# Revit family: VIESSMANN - Vitocell 100-B (CVB.CVBB)
name_source: partatom
category: Wyposażenie mechaniczne
revit_build: Autodesk Revit 2017 (Build: 20160720_1515(x64)
units: mm (PartAtom-declared; Revit-internal decimal feet)

## family parameters
Numer OmniClass = 23.65.35.11.11
Oparty na płaszczyźnie roboczej = Nie
Punkt obliczania pomieszczeń = Nie
Tnij formami wycięć po wczytaniu = Tak
Typ części = Normalny
Tytuł OmniClass = Storage Water Heaters
Współdzielony = Nie
Wymiar okrągłego złącza = Użyj średnicy
Zawsze pionowo = Tak

## types (5) — shared parameters
Autor = https://www.archispace.pl
Klasa efektywności energetycznej = B
Numer identyfikacyjny produktu = 9W241/11-13MC/E
Opis = Podgrzewacz pojemnościowy
Opis indeksowy = 9W241/11-13MC/E
Producent = Viessmann Sp.z.o.o.
Przepływ objętościowy wody grzewczej (dla podanych wydajności stałych) = 3.00 m³/h
Przepływ po stronie wody grzewczej - dolna wężownica = 3.00 m³/h
Przepływ po stronie wody grzewczej - górna wężownica = 3.00 m³/h
Przyłącza - górna wężownica grzewcza = 1"
URL = https://www.viessmann-projektant.pl
Viessmann Kolor 1 = Viessmann Kolor 1
Viessmann Kolor 2 = Viessmann Kolor 2
Viessmann Kolor 3 = Viessmann Kolor 3

## per-type parameters (varying)
- Zbiornik CVBB 950L: Całkowita masa eksploatacyjna z grzałką elektryczną=1342.00 kg; Ciepła woda użytkowa=1 1/4"; Cyrkulacja=1 1/4"; Czas podgrzewu cwu przy tempraturze zasilania wodą grzewczą 70℃=28 min; Czas podgrzewu cwu przy tempraturze zasilania wodą grzewczą 80℃=22 min; Czas podgrzewu cwu przy tempraturze zasilania wodą grzewczą 90℃=18 min; Ilość ciepła dyżurnego=2.48 kWh/24h; Maks. ilość pobierana przy temperaturze na zasilaniu wodą grzewczą 70℃=55; Maks. ilość pobierana przy temperaturze na zasilaniu wodą grzewczą 80℃=60; Maks. ilość pobierana przy temperaturze na zasilaniu wodą grzewczą 90℃=60; Masa całkowita z izolacją cieplną=390.00 kg; Model=Podgrzewacz pojemnościowy Viessmann Vitocell 100-B CVBB 950L / Hot water storage tank Viessmann Vitocell 100-B CVBB 950L; Objętość wody grzewczej - wężownica dolna=33.1 L; Objętość wody grzewczej - wężownica górna=18.6 L; Opory przepływu po stronie wody grzewczej - dolna wężownica=7600.0 Pa; Opory przepływu po stronie wody grzewczej - górna wężownica=19000.0 Pa; Opory przepływu po stronie wody użytkowej=16000.0 Pa; Podział=1062 mm  [stored 3.48425 ft]; Pojemność czesci solarnej Vsol=450 m³; Pojemność części dyżurnej Vaux=500 m³; Pojemność podgrzewacza=950.0 L; Powierzchnia grzewcza - wężownica dolna=3.9 m²; Powierzchnia grzewcza - wężownica górna=2.2 m²; Przepływ objętościowy wody grzewczej (przy podgrzewie cwu z 10 na 45℃) przy temperaturze na zasilaniu wodą grzewczą 50℃ - wężownica dolna=1.03; Przepływ objętościowy wody grzewczej (przy podgrzewie cwu z 10 na 45℃) przy temperaturze na zasilaniu wodą grzewczą 50℃ - wężownica górna=0.76; Przepływ objętościowy wody grzewczej (przy podgrzewie cwu z 10 na 45℃) przy temperaturze na zasilaniu wodą grzewczą 60℃ - wężownica dolna=1.37; Przepływ objętościowy wody grzewczej (przy podgrzewie cwu z 10 na 45℃) przy temperaturze na zasilaniu wodą grzewczą 60℃ - wężownica górna=1.02; Przepływ objętościowy wody grzewczej (przy podgrzewie cwu z 10 na 45℃) przy temperaturze na zasilaniu wodą grzewczą 70℃ - wężownica dolna=1.93; Przepływ objętościowy wody grzewczej (przy podgrzewie cwu z 10 na 45℃) przy temperaturze na zasilaniu wodą grzewczą 70℃ - wężownica górna=1.43; Przepływ objętościowy wody grzewczej (przy podgrzewie cwu z 10 na 45℃) przy temperaturze na zasilaniu wodą grzewczą 80℃ - wężownica dolna=2.48; Przepływ objętościowy wody grzewczej (przy podgrzewie cwu z 10 na 45℃) przy temperaturze na zasilaniu wodą grzewczą 80℃ - wężownica górna=1.84; Przepływ objętościowy wody grzewczej (przy podgrzewie cwu z 10 na 45℃) przy temperaturze na zasilaniu wodą grzewczą 90℃ - wężownica dolna=3.00; Przepływ objętościowy wody grzewczej (przy podgrzewie cwu z 10 na 45℃) przy temperaturze na zasilaniu wodą grzewczą 90℃ - wężownica górna=2.22; Przepływ objętościowy wody grzewczej (przy podgrzewie cwu z 10 na 60℃) przy temperaturze na zasilaniu wodą grzewczą 70℃ - wężownica dolna=0.91; Przepływ objętościowy wody grzewczej (przy podgrzewie cwu z 10 na 60℃) przy temperaturze na zasilaniu wodą grzewczą 70℃ - wężownica górna=0.72; Przepływ objętościowy wody grzewczej (przy podgrzewie cwu z 10 na 60℃) przy temperaturze na zasilaniu wodą grzewczą 80℃ - wężownica dolna=1.22; Przepływ objętościowy wody grzewczej (przy podgrzewie cwu z 10 na 60℃) przy temperaturze na zasilaniu wodą grzewczą 80℃ - wężownica górna=0.96; Przepływ objętościowy wody grzewczej (przy podgrzewie cwu z 10 na 60℃) przy temperaturze na zasilaniu wodą grzewczą 90℃ - wężownica dolna=1.47; Przepływ objętościowy wody grzewczej (przy podgrzewie cwu z 10 na 60℃) przy temperaturze na zasilaniu wodą grzewczą 90℃ - wężownica górna=1.16; Przepływ po stronie wody użytkowej=2.22 m³/h; Przyłącza - dolna wężownica grzewcza=1 1/4"; Przyłącza - grzałka elektryczna=0"; Szerokość - bez izolacji cieplnej=1005 mm  [stored 3.29724 ft]; Szerokość - z izolacją cieplną=1110 mm  [stored 3.64173 ft]; Szerokość z izolacją=1110 mm  [stored 3.64173 ft]; Współczynnik mocy NL przy temperaturze na zasilaniu wodą grzewczą 70℃=10; Współczynnik mocy NL przy temperaturze na zasilaniu wodą grzewczą 80℃=11; Współczynnik mocy NL przy temperaturze na zasilaniu wodą grzewczą 90℃=11; Wydajność krótkotrwała przy temperaturze na zasilaniu wodą grzewczą 70℃=550 L/10min; Wydajność krótkotrwała przy temperaturze na zasilaniu wodą grzewczą 80℃=600 L/10min; Wydajność krótkotrwała przy temperaturze na zasilaniu wodą grzewczą 90℃=600 L/10min; Wydajność stała (przy podgrzewie cwu z 10 na 45℃) i temperaturze na zasilaniu wodą grzewczą 50℃ - wężownica dolna=42000; Wydajność stała (przy podgrzewie cwu z 10 na 45℃) i temperaturze na zasilaniu wodą grzewczą 50℃ - wężownica górna=31000; Wydajność stała (przy podgrzewie cwu z 10 na 45℃) i temperaturze na zasilaniu wodą grzewczą 60℃ - wężownica dolna=56000; Wydajność stała (przy podgrzewie cwu z 10 na 45℃) i temperaturze na zasilaniu wodą grzewczą 60℃ - wężownica górna=41000; Wydajność stała (przy podgrzewie cwu z 10 na 45℃) i temperaturze na zasilaniu wodą grzewczą 70℃ - wężownica dolna=78000; Wydajność stała (przy podgrzewie cwu z 10 na 45℃) i temperaturze na zasilaniu wodą grzewczą 70℃ - wężownica górna=58000; Wydajność stała (przy podgrzewie cwu z 10 na 45℃) i temperaturze na zasilaniu wodą grzewczą 80℃ - wężownica dolna=101000; Wydajność stała (przy podgrzewie cwu z 10 na 45℃) i temperaturze na zasilaniu wodą grzewczą 80℃ - wężownica górna=75000; Wydajność stała (przy podgrzewie cwu z 10 na 45℃) i temperaturze na zasilaniu wodą grzewczą 90℃ - wężownica dolna=122000; Wydajność stała (przy podgrzewie cwu z 10 na 45℃) i temperaturze na zasilaniu wodą grzewczą 90℃ - wężownica górna=90000; Wydajność stała (przy podgrzewie cwu z 10 na 60℃) i temperaturze na zasilaniu wodą grzewczą 70℃ - wężownica dolna=53000; Wydajność stała (przy podgrzewie cwu z 10 na 60℃) i temperaturze na zasilaniu wodą grzewczą 70℃ - wężownica górna=42000; Wydajność stała (przy podgrzewie cwu z 10 na 60℃) i temperaturze na zasilaniu wodą grzewczą 80℃ - wężownica dolna=71000; Wydajność stała (przy podgrzewie cwu z 10 na 60℃) i temperaturze na zasilaniu wodą grzewczą 80℃ - wężownica górna=56000; Wydajność stała (przy podgrzewie cwu z 10 na 60℃) i temperaturze na zasilaniu wodą grzewczą 90℃ - wężownica dolna=85000; Wydajność stała (przy podgrzewie cwu z 10 na 60℃) i temperaturze na zasilaniu wodą grzewczą 90℃ - wężownica górna=67000; Wymiar przechylenia - bez izolacji cieplnej=2286 mm; Wymiar przechylenia - z izolacją cieplną=0 mm  [stored 0 ft]; Wysokość - bez izolacji cieplnej=2103 mm; Wysokość - z izolacją cieplną=2197 mm; Wysokość króćca cwu=2054 mm; Wysokość króćca cyrkulacji=1278 mm  [stored 4.19291 ft]; Wysokość króćca powrotu wody grzewczej=1130 mm  [stored 3.70735 ft]; Wysokość króćca powrotu wody grzewczej inst. solarnej=363 mm  [stored 1.19094 ft]; Wysokość króćca zasilania wodą grzewczą=1760 mm; Wysokość króćca zasilania wodą grzewczą inst. solarnej=983 mm  [stored 3.22507 ft]; Wysokość króćca zimnej wody użytkowej=73 mm  [stored 0.239501 ft]; Wysokość przyłącza grzałki=501 mm  [stored 1.6437 ft]; Wysokość z izolacją=2197 mm; Zimna woda użytkowa=1 1/4"; Średnica - bez izolacji cieplnej=790 mm  [stored 2.59186 ft]; Średnica - z izolacją cieplną=1062 mm  [stored 3.48425 ft]; Średnica z izolacją cieplną=1062 mm  [stored 3.48425 ft]
- Zbiornik CVBB 300L: Całkowita masa eksploatacyjna z grzałką elektryczną=468.00 kg; Ciepła woda użytkowa=1"; Cyrkulacja=1"; Czas podgrzewu cwu przy tempraturze zasilania wodą grzewczą 70℃=30 min; Czas podgrzewu cwu przy tempraturze zasilania wodą grzewczą 80℃=22 min; Czas podgrzewu cwu przy tempraturze zasilania wodą grzewczą 90℃=16 min; Ilość ciepła dyżurnego=1.65 kWh/24h; Maks. ilość pobierana przy temperaturze na zasilaniu wodą grzewczą 70℃=16; Maks. ilość pobierana przy temperaturze na zasilaniu wodą grzewczą 80℃=17; Maks. ilość pobierana przy temperaturze na zasilaniu wodą grzewczą 90℃=17; Masa całkowita z izolacją cieplną=160.00 kg; Model=Podgrzewacz pojemnościowy Viessmann Vitocell 100-B CVBB 300L / Hot water storage tank Viessmann Vitocell 100-B CVBB 300L; Objętość wody grzewczej - wężownica dolna=10.0 L; Objętość wody grzewczej - wężownica górna=6.0 L; Opory przepływu po stronie wody grzewczej - dolna wężownica=18000.0 Pa; Opory przepływu po stronie wody grzewczej - górna wężownica=13000.0 Pa; Opory przepływu po stronie wody użytkowej=200.0 Pa; Podział=667 mm  [stored 2.18832 ft]; Pojemność czesci solarnej Vsol=173 m³; Pojemność części dyżurnej Vaux=127 m³; Pojemność podgrzewacza=300.0 L; Powierzchnia grzewcza - wężownica dolna=1.5 m²; Powierzchnia grzewcza - wężownica górna=0.9 m²; Przepływ objętościowy wody grzewczej (przy podgrzewie cwu z 10 na 45℃) przy temperaturze na zasilaniu wodą grzewczą 50℃ - wężownica dolna=0.44; Przepływ objętościowy wody grzewczej (przy podgrzewie cwu z 10 na 45℃) przy temperaturze na zasilaniu wodą grzewczą 50℃ - wężownica górna=0.27; Przepływ objętościowy wody grzewczej (przy podgrzewie cwu z 10 na 45℃) przy temperaturze na zasilaniu wodą grzewczą 60℃ - wężownica dolna=0.57; Przepływ objętościowy wody grzewczej (przy podgrzewie cwu z 10 na 45℃) przy temperaturze na zasilaniu wodą grzewczą 60℃ - wężownica górna=0.37; Przepływ objętościowy wody grzewczej (przy podgrzewie cwu z 10 na 45℃) przy temperaturze na zasilaniu wodą grzewczą 70℃ - wężownica dolna=0.81; Przepływ objętościowy wody grzewczej (przy podgrzewie cwu z 10 na 45℃) przy temperaturze na zasilaniu wodą grzewczą 70℃ - wężownica górna=0.49; Przepływ objętościowy wody grzewczej (przy podgrzewie cwu z 10 na 45℃) przy temperaturze na zasilaniu wodą grzewczą 80℃ - wężownica dolna=1.08; Przepływ objętościowy wody grzewczej (przy podgrzewie cwu z 10 na 45℃) przy temperaturze na zasilaniu wodą grzewczą 80℃ - wężownica górna=0.64; Przepływ objętościowy wody grzewczej (przy podgrzewie cwu z 10 na 45℃) przy temperaturze na zasilaniu wodą grzewczą 90℃ - wężownica dolna=1.30; Przepływ objętościowy wody grzewczej (przy podgrzewie cwu z 10 na 45℃) przy temperaturze na zasilaniu wodą grzewczą 90℃ - wężownica górna=0.76; Przepływ objętościowy wody grzewczej (przy podgrzewie cwu z 10 na 60℃) przy temperaturze na zasilaniu wodą grzewczą 70℃ - wężownica dolna=395.00; Przepływ objętościowy wody grzewczej (przy podgrzewie cwu z 10 na 60℃) przy temperaturze na zasilaniu wodą grzewczą 70℃ - wężownica górna=258.00; Przepływ objętościowy wody grzewczej (przy podgrzewie cwu z 10 na 60℃) przy temperaturze na zasilaniu wodą grzewczą 80℃ - wężownica dolna=0.58; Przepływ objętościowy wody grzewczej (przy podgrzewie cwu z 10 na 60℃) przy temperaturze na zasilaniu wodą grzewczą 80℃ - wężownica górna=0.34; Przepływ objętościowy wody grzewczej (przy podgrzewie cwu z 10 na 60℃) przy temperaturze na zasilaniu wodą grzewczą 90℃ - wężownica dolna=0.77; Przepływ objętościowy wody grzewczej (przy podgrzewie cwu z 10 na 60℃) przy temperaturze na zasilaniu wodą grzewczą 90℃ - wężownica górna=0.40; Przepływ po stronie wody użytkowej=0.76 m³/h; Przyłącza - dolna wężownica grzewcza=1"; Przyłącza - grzałka elektryczna=1 1/2"; Szerokość - bez izolacji cieplnej=0 mm  [stored 0 ft]; Szerokość - z izolacją cieplną=744 mm  [stored 2.44094 ft]; Szerokość z izolacją=744 mm  [stored 2.44094 ft]; Współczynnik mocy NL przy temperaturze na zasilaniu wodą grzewczą 70℃=1.4; Współczynnik mocy NL przy temperaturze na zasilaniu wodą grzewczą 80℃=1.5; Współczynnik mocy NL przy temperaturze na zasilaniu wodą grzewczą 90℃=1.6; Wydajność krótkotrwała przy temperaturze na zasilaniu wodą grzewczą 70℃=164 L/10min; Wydajność krótkotrwała przy temperaturze na zasilaniu wodą grzewczą 80℃=168 L/10min; Wydajność krótkotrwała przy temperaturze na zasilaniu wodą grzewczą 90℃=173 L/10min; Wydajność stała (przy podgrzewie cwu z 10 na 45℃) i temperaturze na zasilaniu wodą grzewczą 50℃ - wężownica dolna=18000; Wydajność stała (przy podgrzewie cwu z 10 na 45℃) i temperaturze na zasilaniu wodą grzewczą 50℃ - wężownica górna=11000; Wydajność stała (przy podgrzewie cwu z 10 na 45℃) i temperaturze na zasilaniu wodą grzewczą 60℃ - wężownica dolna=23000; Wydajność stała (przy podgrzewie cwu z 10 na 45℃) i temperaturze na zasilaniu wodą grzewczą 60℃ - wężownica górna=15000; Wydajność stała (przy podgrzewie cwu z 10 na 45℃) i temperaturze na zasilaniu wodą grzewczą 70℃ - wężownica dolna=33000; Wydajność stała (przy podgrzewie cwu z 10 na 45℃) i temperaturze na zasilaniu wodą grzewczą 70℃ - wężownica górna=20000; Wydajność stała (przy podgrzewie cwu z 10 na 45℃) i temperaturze na zasilaniu wodą grzewczą 80℃ - wężownica dolna=44000; Wydajność stała (przy podgrzewie cwu z 10 na 45℃) i temperaturze na zasilaniu wodą grzewczą 80℃ - wężownica górna=26000; Wydajność stała (przy podgrzewie cwu z 10 na 45℃) i temperaturze na zasilaniu wodą grzewczą 90℃ - wężownica dolna=53000; Wydajność stała (przy podgrzewie cwu z 10 na 45℃) i temperaturze na zasilaniu wodą grzewczą 90℃ - wężownica górna=31000; Wydajność stała (przy podgrzewie cwu z 10 na 60℃) i temperaturze na zasilaniu wodą grzewczą 70℃ - wężownica dolna=23000; Wydajność stała (przy podgrzewie cwu z 10 na 60℃) i temperaturze na zasilaniu wodą grzewczą 70℃ - wężownica górna=15000; Wydajność stała (przy podgrzewie cwu z 10 na 60℃) i temperaturze na zasilaniu wodą grzewczą 80℃ - wężownica dolna=34000; Wydajność stała (przy podgrzewie cwu z 10 na 60℃) i temperaturze na zasilaniu wodą grzewczą 80℃ - wężownica górna=20000; Wydajność stała (przy podgrzewie cwu z 10 na 60℃) i temperaturze na zasilaniu wodą grzewczą 90℃ - wężownica dolna=45000; Wydajność stała (przy podgrzewie cwu z 10 na 60℃) i temperaturze na zasilaniu wodą grzewczą 90℃ - wężownica górna=23000; Wymiar przechylenia - bez izolacji cieplnej=0 mm  [stored 0 ft]; Wymiar przechylenia - z izolacją cieplną=1825 mm; Wysokość - bez izolacji cieplnej=0 mm  [stored 0 ft]; Wysokość - z izolacją cieplną=1734 mm; Wysokość króćca cwu=1600 mm; Wysokość króćca cyrkulacji=1115 mm  [stored 3.65814 ft]; Wysokość króćca powrotu wody grzewczej=995 mm  [stored 3.26444 ft]; Wysokość króćca powrotu wody grzewczej inst. solarnej=260 mm  [stored 0.853018 ft]; Wysokość króćca zasilania wodą grzewczą=1355 mm  [stored 4.44554 ft]; Wysokość króćca zasilania wodą grzewczą inst. solarnej=875 mm  [stored 2.87073 ft]; Wysokość króćca zimnej wody użytkowej=76 mm  [stored 0.249344 ft]; Wysokość przyłącza grzałki=333 mm  [stored 1.09252 ft]; Wysokość z izolacją=1734 mm; Zimna woda użytkowa=1"; Średnica - bez izolacji cieplnej=0 mm  [stored 0 ft]; Średnica - z izolacją cieplną=667 mm  [stored 2.18832 ft]; Średnica z izolacją cieplną=667 mm  [stored 2.18832 ft]
- Zbiornik CVB 500L: Całkowita masa eksploatacyjna z grzałką elektryczną=707.00 kg; Ciepła woda użytkowa=1 1/4"; Cyrkulacja=1"; Czas podgrzewu cwu przy tempraturze zasilania wodą grzewczą 70℃=37 min; Czas podgrzewu cwu przy tempraturze zasilania wodą grzewczą 80℃=24 min; Czas podgrzewu cwu przy tempraturze zasilania wodą grzewczą 90℃=19 min; Ilość ciepła dyżurnego=1.95 kWh/24h; Maks. ilość pobierana przy temperaturze na zasilaniu wodą grzewczą 70℃=30; Maks. ilość pobierana przy temperaturze na zasilaniu wodą grzewczą 80℃=32; Maks. ilość pobierana przy temperaturze na zasilaniu wodą grzewczą 90℃=32; Masa całkowita z izolacją cieplną=205.00 kg; Model=Podgrzewacz pojemnościowy Viessmann Vitocell 100-B CVB 500L / Hot water storage tank Viessmann Vitocell 100-B CVB 500L; Objętość wody grzewczej - wężownica dolna=12.5 L; Objętość wody grzewczej - wężownica górna=9.0 L; Opory przepływu po stronie wody grzewczej - dolna wężownica=20000.0 Pa; Opory przepływu po stronie wody grzewczej - górna wężownica=18000.0 Pa; Opory przepływu po stronie wody użytkowej=250.0 Pa; Podział=859 mm  [stored 2.81824 ft]; Pojemność czesci solarnej Vsol=269 m³; Pojemność części dyżurnej Vaux=231 m³; Pojemność podgrzewacza=500.0 L; Powierzchnia grzewcza - wężownica dolna=1.9 m²; Powierzchnia grzewcza - wężownica górna=1.4 m²; Przepływ objętościowy wody grzewczej (przy podgrzewie cwu z 10 na 45℃) przy temperaturze na zasilaniu wodą grzewczą 50℃ - wężownica dolna=0.59; Przepływ objętościowy wody grzewczej (przy podgrzewie cwu z 10 na 45℃) przy temperaturze na zasilaniu wodą grzewczą 50℃ - wężownica górna=0.39; Przepływ objętościowy wody grzewczej (przy podgrzewie cwu z 10 na 45℃) przy temperaturze na zasilaniu wodą grzewczą 60℃ - wężownica dolna=0.79; Przepływ objętościowy wody grzewczej (przy podgrzewie cwu z 10 na 45℃) przy temperaturze na zasilaniu wodą grzewczą 60℃ - wężownica górna=0.54; Przepływ objętościowy wody grzewczej (przy podgrzewie cwu z 10 na 45℃) przy temperaturze na zasilaniu wodą grzewczą 70℃ - wężownica dolna=1.11; Przepływ objętościowy wody grzewczej (przy podgrzewie cwu z 10 na 45℃) przy temperaturze na zasilaniu wodą grzewczą 70℃ - wężownica górna=0.74; Przepływ objętościowy wody grzewczej (przy podgrzewie cwu z 10 na 45℃) przy temperaturze na zasilaniu wodą grzewczą 80℃ - wężownica dolna=1.43; Przepływ objętościowy wody grzewczej (przy podgrzewie cwu z 10 na 45℃) przy temperaturze na zasilaniu wodą grzewczą 80℃ - wężownica górna=0.98; Przepływ objętościowy wody grzewczej (przy podgrzewie cwu z 10 na 45℃) przy temperaturze na zasilaniu wodą grzewczą 90℃ - wężownica dolna=1.72; Przepływ objętościowy wody grzewczej (przy podgrzewie cwu z 10 na 45℃) przy temperaturze na zasilaniu wodą grzewczą 90℃ - wężownica górna=1.15; Przepływ objętościowy wody grzewczej (przy podgrzewie cwu z 10 na 60℃) przy temperaturze na zasilaniu wodą grzewczą 70℃ - wężownica dolna=0.57; Przepływ objętościowy wody grzewczej (przy podgrzewie cwu z 10 na 60℃) przy temperaturze na zasilaniu wodą grzewczą 70℃ - wężownica górna=0.38; Przepływ objętościowy wody grzewczej (przy podgrzewie cwu z 10 na 60℃) przy temperaturze na zasilaniu wodą grzewczą 80℃ - wężownica dolna=0.76; Przepływ objętościowy wody grzewczej (przy podgrzewie cwu z 10 na 60℃) przy temperaturze na zasilaniu wodą grzewczą 80℃ - wężownica górna=0.52; Przepływ objętościowy wody grzewczej (przy podgrzewie cwu z 10 na 60℃) przy temperaturze na zasilaniu wodą grzewczą 90℃ - wężownica dolna=0.91; Przepływ objętościowy wody grzewczej (przy podgrzewie cwu z 10 na 60℃) przy temperaturze na zasilaniu wodą grzewczą 90℃ - wężownica górna=0.62; Przepływ po stronie wody użytkowej=1.15 m³/h; Przyłącza - dolna wężownica grzewcza=1"; Przyłącza - grzałka elektryczna=1 1/2"; Szerokość - bez izolacji cieplnej=881 mm  [stored 2.89042 ft]; Szerokość - z izolacją cieplną=923 mm  [stored 3.02822 ft]; Szerokość z izolacją=923 mm  [stored 3.02822 ft]; Współczynnik mocy NL przy temperaturze na zasilaniu wodą grzewczą 70℃=5; Współczynnik mocy NL przy temperaturze na zasilaniu wodą grzewczą 80℃=6; Współczynnik mocy NL przy temperaturze na zasilaniu wodą grzewczą 90℃=6; Wydajność krótkotrwała przy temperaturze na zasilaniu wodą grzewczą 70℃=299 L/10min; Wydajność krótkotrwała przy temperaturze na zasilaniu wodą grzewczą 80℃=319 L/10min; Wydajność krótkotrwała przy temperaturze na zasilaniu wodą grzewczą 90℃=319 L/10min; Wydajność stała (przy podgrzewie cwu z 10 na 45℃) i temperaturze na zasilaniu wodą grzewczą 50℃ - wężownica dolna=24000; Wydajność stała (przy podgrzewie cwu z 10 na 45℃) i temperaturze na zasilaniu wodą grzewczą 50℃ - wężownica górna=16000; Wydajność stała (przy podgrzewie cwu z 10 na 45℃) i temperaturze na zasilaniu wodą grzewczą 60℃ - wężownica dolna=32000; Wydajność stała (przy podgrzewie cwu z 10 na 45℃) i temperaturze na zasilaniu wodą grzewczą 60℃ - wężownica górna=22000; Wydajność stała (przy podgrzewie cwu z 10 na 45℃) i temperaturze na zasilaniu wodą grzewczą 70℃ - wężownica dolna=45000; Wydajność stała (przy podgrzewie cwu z 10 na 45℃) i temperaturze na zasilaniu wodą grzewczą 70℃ - wężownica górna=30000; Wydajność stała (przy podgrzewie cwu z 10 na 45℃) i temperaturze na zasilaniu wodą grzewczą 80℃ - wężownica dolna=58000; Wydajność stała (przy podgrzewie cwu z 10 na 45℃) i temperaturze na zasilaniu wodą grzewczą 80℃ - wężownica górna=40000; Wydajność stała (przy podgrzewie cwu z 10 na 45℃) i temperaturze na zasilaniu wodą grzewczą 90℃ - wężownica dolna=70000; Wydajność stała (przy podgrzewie cwu z 10 na 45℃) i temperaturze na zasilaniu wodą grzewczą 90℃ - wężownica górna=47000; Wydajność stała (przy podgrzewie cwu z 10 na 60℃) i temperaturze na zasilaniu wodą grzewczą 70℃ - wężownica dolna=33000; Wydajność stała (przy podgrzewie cwu z 10 na 60℃) i temperaturze na zasilaniu wodą grzewczą 70℃ - wężownica górna=22000; Wydajność stała (przy podgrzewie cwu z 10 na 60℃) i temperaturze na zasilaniu wodą grzewczą 80℃ - wężownica dolna=44000; Wydajność stała (przy podgrzewie cwu z 10 na 60℃) i temperaturze na zasilaniu wodą grzewczą 80℃ - wężownica górna=30000; Wydajność stała (przy podgrzewie cwu z 10 na 60℃) i temperaturze na zasilaniu wodą grzewczą 90℃ - wężownica dolna=53000; Wydajność stała (przy podgrzewie cwu z 10 na 60℃) i temperaturze na zasilaniu wodą grzewczą 90℃ - wężownica górna=36000; Wymiar przechylenia - bez izolacji cieplnej=1860 mm; Wymiar przechylenia - z izolacją cieplną=0 mm  [stored 0 ft]; Wysokość - bez izolacji cieplnej=1844 mm; Wysokość - z izolacją cieplną=1948 mm; Wysokość króćca cwu=1784 mm; Wysokość króćca cyrkulacji=1230 mm  [stored 4.03543 ft]; Wysokość króćca powrotu wody grzewczej=1044 mm; Wysokość króćca powrotu wody grzewczej inst. solarnej=349 mm  [stored 1.14501 ft]; Wysokość króćca zasilania wodą grzewczą=1444 mm  [stored 4.73753 ft]; Wysokość króćca zasilania wodą grzewczą inst. solarnej=924 mm  [stored 3.0315 ft]; Wysokość króćca zimnej wody użytkowej=107 mm  [stored 0.35105 ft]; Wysokość przyłącza grzałki=422 mm  [stored 1.38451 ft]; Wysokość z izolacją=1948 mm; Zimna woda użytkowa=1 1/4"; Średnica - bez izolacji cieplnej=650 mm  [stored 2.13255 ft]; Średnica - z izolacją cieplną=859 mm  [stored 2.81824 ft]; Średnica z izolacją cieplną=859 mm  [stored 2.81824 ft]
- Zbiornik CVB 400L: Całkowita masa eksploatacyjna z grzałką elektryczną=569.00 kg; Ciepła woda użytkowa=1 1/4"; Cyrkulacja=1"; Czas podgrzewu cwu przy tempraturze zasilania wodą grzewczą 70℃=36 min; Czas podgrzewu cwu przy tempraturze zasilania wodą grzewczą 80℃=23 min; Czas podgrzewu cwu przy tempraturze zasilania wodą grzewczą 90℃=17 min; Ilość ciepła dyżurnego=1.80 kWh/24h; Maks. ilość pobierana przy temperaturze na zasilaniu wodą grzewczą 70℃=21; Maks. ilość pobierana przy temperaturze na zasilaniu wodą grzewczą 80℃=23; Maks. ilość pobierana przy temperaturze na zasilaniu wodą grzewczą 90℃=23; Masa całkowita z izolacją cieplną=167.00 kg; Model=Podgrzewacz pojemnościowy Viessmann Vitocell 100-B CVB 400L / Hot water storage tank Viessmann Vitocell 100-B CVB 400L; Objętość wody grzewczej - wężownica dolna=10.5 L; Objętość wody grzewczej - wężownica górna=6.5 L; Opory przepływu po stronie wody grzewczej - dolna wężownica=12000.0 Pa; Opory przepływu po stronie wody grzewczej - górna wężownica=18000.0 Pa; Opory przepływu po stronie wody użytkowej=200.0 Pa; Podział=859 mm  [stored 2.81824 ft]; Pojemność czesci solarnej Vsol=233 m³; Pojemność części dyżurnej Vaux=167 m³; Pojemność podgrzewacza=400.0 L; Powierzchnia grzewcza - wężownica dolna=1.5 m²; Powierzchnia grzewcza - wężownica górna=1.0 m²; Przepływ objętościowy wody grzewczej (przy podgrzewie cwu z 10 na 45℃) przy temperaturze na zasilaniu wodą grzewczą 50℃ - wężownica dolna=0.32; Przepływ objętościowy wody grzewczej (przy podgrzewie cwu z 10 na 45℃) przy temperaturze na zasilaniu wodą grzewczą 50℃ - wężownica górna=0.25; Przepływ objętościowy wody grzewczej (przy podgrzewie cwu z 10 na 45℃) przy temperaturze na zasilaniu wodą grzewczą 60℃ - wężownica dolna=0.66; Przepływ objętościowy wody grzewczej (przy podgrzewie cwu z 10 na 45℃) przy temperaturze na zasilaniu wodą grzewczą 60℃ - wężownica górna=0.42; Przepływ objętościowy wody grzewczej (przy podgrzewie cwu z 10 na 45℃) przy temperaturze na zasilaniu wodą grzewczą 70℃ - wężownica dolna=0.96; Przepływ objętościowy wody grzewczej (przy podgrzewie cwu z 10 na 45℃) przy temperaturze na zasilaniu wodą grzewczą 70℃ - wężownica górna=0.61; Przepływ objętościowy wody grzewczej (przy podgrzewie cwu z 10 na 45℃) przy temperaturze na zasilaniu wodą grzewczą 80℃ - wężownica dolna=1.28; Przepływ objętościowy wody grzewczej (przy podgrzewie cwu z 10 na 45℃) przy temperaturze na zasilaniu wodą grzewczą 80℃ - wężownica górna=0.81; Przepływ objętościowy wody grzewczej (przy podgrzewie cwu z 10 na 45℃) przy temperaturze na zasilaniu wodą grzewczą 90℃ - wężownica dolna=1.55; Przepływ objętościowy wody grzewczej (przy podgrzewie cwu z 10 na 45℃) przy temperaturze na zasilaniu wodą grzewczą 90℃ - wężownica górna=1.03; Przepływ objętościowy wody grzewczej (przy podgrzewie cwu z 10 na 60℃) przy temperaturze na zasilaniu wodą grzewczą 70℃ - wężownica dolna=0.50; Przepływ objętościowy wody grzewczej (przy podgrzewie cwu z 10 na 60℃) przy temperaturze na zasilaniu wodą grzewczą 70℃ - wężownica górna=0.31; Przepływ objętościowy wody grzewczej (przy podgrzewie cwu z 10 na 60℃) przy temperaturze na zasilaniu wodą grzewczą 80℃ - wężownica dolna=0.72; Przepływ objętościowy wody grzewczej (przy podgrzewie cwu z 10 na 60℃) przy temperaturze na zasilaniu wodą grzewczą 80℃ - wężownica górna=0.46; Przepływ objętościowy wody grzewczej (przy podgrzewie cwu z 10 na 60℃) przy temperaturze na zasilaniu wodą grzewczą 90℃ - wężownica dolna=0.96; Przepływ objętościowy wody grzewczej (przy podgrzewie cwu z 10 na 60℃) przy temperaturze na zasilaniu wodą grzewczą 90℃ - wężownica górna=0.62; Przepływ po stronie wody użytkowej=1.03 m³/h; Przyłącza - dolna wężownica grzewcza=1"; Przyłącza - grzałka elektryczna=1 1/2"; Szerokość - bez izolacji cieplnej=881 mm  [stored 2.89042 ft]; Szerokość - z izolacją cieplną=923 mm  [stored 3.02822 ft]; Szerokość z izolacją=923 mm  [stored 3.02822 ft]; Współczynnik mocy NL przy temperaturze na zasilaniu wodą grzewczą 70℃=2.5; Współczynnik mocy NL przy temperaturze na zasilaniu wodą grzewczą 80℃=3; Współczynnik mocy NL przy temperaturze na zasilaniu wodą grzewczą 90℃=3; Wydajność krótkotrwała przy temperaturze na zasilaniu wodą grzewczą 70℃=210 L/10min; Wydajność krótkotrwała przy temperaturze na zasilaniu wodą grzewczą 80℃=230 L/10min; Wydajność krótkotrwała przy temperaturze na zasilaniu wodą grzewczą 90℃=230 L/10min; Wydajność stała (przy podgrzewie cwu z 10 na 45℃) i temperaturze na zasilaniu wodą grzewczą 50℃ - wężownica dolna=13000; Wydajność stała (przy podgrzewie cwu z 10 na 45℃) i temperaturze na zasilaniu wodą grzewczą 50℃ - wężownica górna=10000; Wydajność stała (przy podgrzewie cwu z 10 na 45℃) i temperaturze na zasilaniu wodą grzewczą 60℃ - wężownica dolna=27000; Wydajność stała (przy podgrzewie cwu z 10 na 45℃) i temperaturze na zasilaniu wodą grzewczą 60℃ - wężownica górna=17000; Wydajność stała (przy podgrzewie cwu z 10 na 45℃) i temperaturze na zasilaniu wodą grzewczą 70℃ - wężownica dolna=39000; Wydajność stała (przy podgrzewie cwu z 10 na 45℃) i temperaturze na zasilaniu wodą grzewczą 70℃ - wężownica górna=25000; Wydajność stała (przy podgrzewie cwu z 10 na 45℃) i temperaturze na zasilaniu wodą grzewczą 80℃ - wężownica dolna=52000; Wydajność stała (przy podgrzewie cwu z 10 na 45℃) i temperaturze na zasilaniu wodą grzewczą 80℃ - wężownica górna=33000; Wydajność stała (przy podgrzewie cwu z 10 na 45℃) i temperaturze na zasilaniu wodą grzewczą 90℃ - wężownica dolna=63000; Wydajność stała (przy podgrzewie cwu z 10 na 45℃) i temperaturze na zasilaniu wodą grzewczą 90℃ - wężownica górna=42000; Wydajność stała (przy podgrzewie cwu z 10 na 60℃) i temperaturze na zasilaniu wodą grzewczą 70℃ - wężownica dolna=29000; Wydajność stała (przy podgrzewie cwu z 10 na 60℃) i temperaturze na zasilaniu wodą grzewczą 70℃ - wężownica górna=18000; Wydajność stała (przy podgrzewie cwu z 10 na 60℃) i temperaturze na zasilaniu wodą grzewczą 80℃ - wężownica dolna=42000; Wydajność stała (przy podgrzewie cwu z 10 na 60℃) i temperaturze na zasilaniu wodą grzewczą 80℃ - wężownica górna=27000; Wydajność stała (przy podgrzewie cwu z 10 na 60℃) i temperaturze na zasilaniu wodą grzewczą 90℃ - wężownica dolna=56000; Wydajność stała (przy podgrzewie cwu z 10 na 60℃) i temperaturze na zasilaniu wodą grzewczą 90℃ - wężownica górna=36000; Wymiar przechylenia - bez izolacji cieplnej=1550 mm; Wymiar przechylenia - z izolacją cieplną=0 mm  [stored 0 ft]; Wysokość - bez izolacji cieplnej=1844 mm; Wysokość - z izolacją cieplną=1948 mm; Wysokość króćca cwu=1458 mm  [stored 4.78346 ft]; Wysokość króćca cyrkulacji=1044 mm; Wysokość króćca powrotu wody grzewczej=924 mm  [stored 3.0315 ft]; Wysokość króćca powrotu wody grzewczej inst. solarnej=349 mm  [stored 1.14501 ft]; Wysokość króćca zasilania wodą grzewczą=1204 mm  [stored 3.95013 ft]; Wysokość króćca zasilania wodą grzewczą inst. solarnej=804 mm  [stored 2.6378 ft]; Wysokość króćca zimnej wody użytkowej=107 mm  [stored 0.35105 ft]; Wysokość przyłącza grzałki=422 mm  [stored 1.38451 ft]; Wysokość z izolacją=1624 mm; Zimna woda użytkowa=1 1/4"; Średnica - bez izolacji cieplnej=650 mm  [stored 2.13255 ft]; Średnica - z izolacją cieplną=859 mm  [stored 2.81824 ft]; Średnica z izolacją cieplną=859 mm  [stored 2.81824 ft]
- Zbiornik CVBB 750L: Całkowita masa eksploatacyjna z grzałką elektryczną=1072.00 kg; Ciepła woda użytkowa=1 1/4"; Cyrkulacja=1 1/4"; Czas podgrzewu cwu przy tempraturze zasilania wodą grzewczą 70℃=26 min; Czas podgrzewu cwu przy tempraturze zasilania wodą grzewczą 80℃=21 min; Czas podgrzewu cwu przy tempraturze zasilania wodą grzewczą 90℃=17 min; Ilość ciepła dyżurnego=2.28 kWh/24h; Maks. ilość pobierana przy temperaturze na zasilaniu wodą grzewczą 70℃=40; Maks. ilość pobierana przy temperaturze na zasilaniu wodą grzewczą 80℃=44; Maks. ilość pobierana przy temperaturze na zasilaniu wodą grzewczą 90℃=44; Masa całkowita z izolacją cieplną=320.00 kg; Model=Podgrzewacz pojemnościowy Viessmann Vitocell 100-B CVBB 750L / Hot water storage tank Viessmann Vitocell 100-B CVBB 750L; Objętość wody grzewczej - wężownica dolna=29.7 L; Objętość wody grzewczej - wężownica górna=13.8 L; Opory przepływu po stronie wody grzewczej - dolna wężownica=7600.0 Pa; Opory przepływu po stronie wody grzewczej - górna wężownica=19000.0 Pa; Opory przepływu po stronie wody użytkowej=700.0 Pa; Podział=1062 mm  [stored 3.48425 ft]; Pojemność czesci solarnej Vsol=385 m³; Pojemność części dyżurnej Vaux=365 m³; Pojemność podgrzewacza=750.0 L; Powierzchnia grzewcza - wężownica dolna=3.5 m²; Powierzchnia grzewcza - wężownica górna=1.6 m²; Przepływ objętościowy wody grzewczej (przy podgrzewie cwu z 10 na 45℃) przy temperaturze na zasilaniu wodą grzewczą 50℃ - wężownica dolna=0.96; Przepływ objętościowy wody grzewczej (przy podgrzewie cwu z 10 na 45℃) przy temperaturze na zasilaniu wodą grzewczą 50℃ - wężownica górna=0.64; Przepływ objętościowy wody grzewczej (przy podgrzewie cwu z 10 na 45℃) przy temperaturze na zasilaniu wodą grzewczą 60℃ - wężownica dolna=1.28; Przepływ objętościowy wody grzewczej (przy podgrzewie cwu z 10 na 45℃) przy temperaturze na zasilaniu wodą grzewczą 60℃ - wężownica górna=0.85; Przepływ objętościowy wody grzewczej (przy podgrzewie cwu z 10 na 45℃) przy temperaturze na zasilaniu wodą grzewczą 70℃ - wężownica dolna=1.79; Przepływ objętościowy wody grzewczej (przy podgrzewie cwu z 10 na 45℃) przy temperaturze na zasilaniu wodą grzewczą 70℃ - wężownica górna=1.20; Przepływ objętościowy wody grzewczej (przy podgrzewie cwu z 10 na 45℃) przy temperaturze na zasilaniu wodą grzewczą 80℃ - wężownica dolna=2.31; Przepływ objętościowy wody grzewczej (przy podgrzewie cwu z 10 na 45℃) przy temperaturze na zasilaniu wodą grzewczą 80℃ - wężownica górna=1.55; Przepływ objętościowy wody grzewczej (przy podgrzewie cwu z 10 na 45℃) przy temperaturze na zasilaniu wodą grzewczą 90℃ - wężownica dolna=2.79; Przepływ objętościowy wody grzewczej (przy podgrzewie cwu z 10 na 45℃) przy temperaturze na zasilaniu wodą grzewczą 90℃ - wężownica górna=1.87; Przepływ objętościowy wody grzewczej (przy podgrzewie cwu z 10 na 60℃) przy temperaturze na zasilaniu wodą grzewczą 70℃ - wężownica dolna=0.85; Przepływ objętościowy wody grzewczej (przy podgrzewie cwu z 10 na 60℃) przy temperaturze na zasilaniu wodą grzewczą 70℃ - wężownica górna=0.63; Przepływ objętościowy wody grzewczej (przy podgrzewie cwu z 10 na 60℃) przy temperaturze na zasilaniu wodą grzewczą 80℃ - wężownica dolna=1.13; Przepływ objętościowy wody grzewczej (przy podgrzewie cwu z 10 na 60℃) przy temperaturze na zasilaniu wodą grzewczą 80℃ - wężownica górna=0.84; Przepływ objętościowy wody grzewczej (przy podgrzewie cwu z 10 na 60℃) przy temperaturze na zasilaniu wodą grzewczą 90℃ - wężownica dolna=1.36; Przepływ objętościowy wody grzewczej (przy podgrzewie cwu z 10 na 60℃) przy temperaturze na zasilaniu wodą grzewczą 90℃ - wężownica górna=1.01; Przepływ po stronie wody użytkowej=1.87 m³/h; Przyłącza - dolna wężownica grzewcza=1 1/4"; Przyłącza - grzałka elektryczna=0"; Szerokość - bez izolacji cieplnej=1005 mm  [stored 3.29724 ft]; Szerokość - z izolacją cieplną=1110 mm  [stored 3.64173 ft]; Szerokość z izolacją=1110 mm  [stored 3.64173 ft]; Współczynnik mocy NL przy temperaturze na zasilaniu wodą grzewczą 70℃=7; Współczynnik mocy NL przy temperaturze na zasilaniu wodą grzewczą 80℃=8; Współczynnik mocy NL przy temperaturze na zasilaniu wodą grzewczą 90℃=8; Wydajność krótkotrwała przy temperaturze na zasilaniu wodą grzewczą 70℃=400 L/10min; Wydajność krótkotrwała przy temperaturze na zasilaniu wodą grzewczą 80℃=438 L/10min; Wydajność krótkotrwała przy temperaturze na zasilaniu wodą grzewczą 90℃=438 L/10min; Wydajność stała (przy podgrzewie cwu z 10 na 45℃) i temperaturze na zasilaniu wodą grzewczą 50℃ - wężownica dolna=39000; Wydajność stała (przy podgrzewie cwu z 10 na 45℃) i temperaturze na zasilaniu wodą grzewczą 50℃ - wężownica górna=26000; Wydajność stała (przy podgrzewie cwu z 10 na 45℃) i temperaturze na zasilaniu wodą grzewczą 60℃ - wężownica dolna=52000; Wydajność stała (przy podgrzewie cwu z 10 na 45℃) i temperaturze na zasilaniu wodą grzewczą 60℃ - wężownica górna=35000; Wydajność stała (przy podgrzewie cwu z 10 na 45℃) i temperaturze na zasilaniu wodą grzewczą 70℃ - wężownica dolna=73000; Wydajność stała (przy podgrzewie cwu z 10 na 45℃) i temperaturze na zasilaniu wodą grzewczą 70℃ - wężownica górna=49000; Wydajność stała (przy podgrzewie cwu z 10 na 45℃) i temperaturze na zasilaniu wodą grzewczą 80℃ - wężownica dolna=94000; Wydajność stała (przy podgrzewie cwu z 10 na 45℃) i temperaturze na zasilaniu wodą grzewczą 80℃ - wężownica górna=63000; Wydajność stała (przy podgrzewie cwu z 10 na 45℃) i temperaturze na zasilaniu wodą grzewczą 90℃ - wężownica dolna=114000; Wydajność stała (przy podgrzewie cwu z 10 na 45℃) i temperaturze na zasilaniu wodą grzewczą 90℃ - wężownica górna=76000; Wydajność stała (przy podgrzewie cwu z 10 na 60℃) i temperaturze na zasilaniu wodą grzewczą 70℃ - wężownica dolna=49000; Wydajność stała (przy podgrzewie cwu z 10 na 60℃) i temperaturze na zasilaniu wodą grzewczą 70℃ - wężownica górna=37000; Wydajność stała (przy podgrzewie cwu z 10 na 60℃) i temperaturze na zasilaniu wodą grzewczą 80℃ - wężownica dolna=66000; Wydajność stała (przy podgrzewie cwu z 10 na 60℃) i temperaturze na zasilaniu wodą grzewczą 80℃ - wężownica górna=49000; Wydajność stała (przy podgrzewie cwu z 10 na 60℃) i temperaturze na zasilaniu wodą grzewczą 90℃ - wężownica dolna=79000; Wydajność stała (przy podgrzewie cwu z 10 na 60℃) i temperaturze na zasilaniu wodą grzewczą 90℃ - wężownica górna=59000; Wymiar przechylenia - bez izolacji cieplnej=1980 mm; Wymiar przechylenia - z izolacją cieplną=0 mm  [stored 0 ft]; Wysokość - bez izolacji cieplnej=1797 mm; Wysokość - z izolacją cieplną=1897 mm; Wysokość króćca cwu=1749 mm; Wysokość króćca cyrkulacji=1175 mm; Wysokość króćca powrotu wody grzewczej=1044 mm; Wysokość króćca powrotu wody grzewczej inst. solarnej=373 mm  [stored 1.22375 ft]; Wysokość króćca zasilania wodą grzewczą=1464 mm; Wysokość króćca zasilania wodą grzewczą inst. solarnej=912 mm  [stored 2.99213 ft]; Wysokość króćca zimnej wody użytkowej=74 mm  [stored 0.242782 ft]; Wysokość przyłącza grzałki=509 mm  [stored 1.66995 ft]; Wysokość z izolacją=1897 mm; Zimna woda użytkowa=1 1/4"; Średnica - bez izolacji cieplnej=790 mm  [stored 2.59186 ft]; Średnica - z izolacją cieplną=1062 mm  [stored 3.48425 ft]; Średnica z izolacją cieplną=1062 mm  [stored 3.48425 ft]

note: source unit labels omitted for Maks. ilość pobierana przy temperaturze na zasilaniu wodą grzewczą 70℃, Maks. ilość pobierana przy temperaturze na zasilaniu wodą grzewczą 80℃, Maks. ilość pobierana przy temperaturze na zasilaniu wodą grzewczą 90℃, Przepływ objętościowy wody grzewczej (przy podgrzewie cwu z 10 na 45℃) przy temperaturze na zasilaniu wodą grzewczą 50℃ - wężownica dolna, Przepływ objętościowy wody grzewczej (przy podgrzewie cwu z 10 na 45℃) przy temperaturze na zasilaniu wodą grzewczą 50℃ - wężownica górna, Przepływ objętościowy wody grzewczej (przy podgrzewie cwu z 10 na 45℃) przy temperaturze na zasilaniu wodą grzewczą 60℃ - wężownica dolna, Przepływ objętościowy wody grzewczej (przy podgrzewie cwu z 10 na 45℃) przy temperaturze na zasilaniu wodą grzewczą 60℃ - wężownica górna, Przepływ objętościowy wody grzewczej (przy podgrzewie cwu z 10 na 45℃) przy temperaturze na zasilaniu wodą grzewczą 70℃ - wężownica dolna, Przepływ objętościowy wody grzewczej (przy podgrzewie cwu z 10 na 45℃) przy temperaturze na zasilaniu wodą grzewczą 70℃ - wężownica górna, Przepływ objętościowy wody grzewczej (przy podgrzewie cwu z 10 na 45℃) przy temperaturze na zasilaniu wodą grzewczą 80℃ - wężownica dolna, Przepływ objętościowy wody grzewczej (przy podgrzewie cwu z 10 na 45℃) przy temperaturze na zasilaniu wodą grzewczą 80℃ - wężownica górna, Przepływ objętościowy wody grzewczej (przy podgrzewie cwu z 10 na 45℃) przy temperaturze na zasilaniu wodą grzewczą 90℃ - wężownica dolna, Przepływ objętościowy wody grzewczej (przy podgrzewie cwu z 10 na 45℃) przy temperaturze na zasilaniu wodą grzewczą 90℃ - wężownica górna, Przepływ objętościowy wody grzewczej (przy podgrzewie cwu z 10 na 60℃) przy temperaturze na zasilaniu wodą grzewczą 70℃ - wężownica dolna, Przepływ objętościowy wody grzewczej (przy podgrzewie cwu z 10 na 60℃) przy temperaturze na zasilaniu wodą grzewczą 70℃ - wężownica górna, Przepływ objętościowy wody grzewczej (przy podgrzewie cwu z 10 na 60℃) przy temperaturze na zasilaniu wodą grzewczą 80℃ - wężownica dolna, Przepływ objętościowy wody grzewczej (przy podgrzewie cwu z 10 na 60℃) przy temperaturze na zasilaniu wodą grzewczą 80℃ - wężownica górna, Przepływ objętościowy wody grzewczej (przy podgrzewie cwu z 10 na 60℃) przy temperaturze na zasilaniu wodą grzewczą 90℃ - wężownica dolna, Przepływ objętościowy wody grzewczej (przy podgrzewie cwu z 10 na 60℃) przy temperaturze na zasilaniu wodą grzewczą 90℃ - wężownica górna, Wydajność stała (przy podgrzewie cwu z 10 na 45℃) i temperaturze na zasilaniu wodą grzewczą 50℃ - wężownica dolna, Wydajność stała (przy podgrzewie cwu z 10 na 45℃) i temperaturze na zasilaniu wodą grzewczą 50℃ - wężownica górna, Wydajność stała (przy podgrzewie cwu z 10 na 45℃) i temperaturze na zasilaniu wodą grzewczą 60℃ - wężownica dolna, Wydajność stała (przy podgrzewie cwu z 10 na 45℃) i temperaturze na zasilaniu wodą grzewczą 60℃ - wężownica górna, Wydajność stała (przy podgrzewie cwu z 10 na 45℃) i temperaturze na zasilaniu wodą grzewczą 70℃ - wężownica dolna, Wydajność stała (przy podgrzewie cwu z 10 na 45℃) i temperaturze na zasilaniu wodą grzewczą 70℃ - wężownica górna, Wydajność stała (przy podgrzewie cwu z 10 na 45℃) i temperaturze na zasilaniu wodą grzewczą 80℃ - wężownica dolna, Wydajność stała (przy podgrzewie cwu z 10 na 45℃) i temperaturze na zasilaniu wodą grzewczą 80℃ - wężownica górna, Wydajność stała (przy podgrzewie cwu z 10 na 45℃) i temperaturze na zasilaniu wodą grzewczą 90℃ - wężownica dolna, Wydajność stała (przy podgrzewie cwu z 10 na 45℃) i temperaturze na zasilaniu wodą grzewczą 90℃ - wężownica górna, Wydajność stała (przy podgrzewie cwu z 10 na 60℃) i temperaturze na zasilaniu wodą grzewczą 70℃ - wężownica dolna, Wydajność stała (przy podgrzewie cwu z 10 na 60℃) i temperaturze na zasilaniu wodą grzewczą 70℃ - wężownica górna, Wydajność stała (przy podgrzewie cwu z 10 na 60℃) i temperaturze na zasilaniu wodą grzewczą 80℃ - wężownica dolna, Wydajność stała (przy podgrzewie cwu z 10 na 60℃) i temperaturze na zasilaniu wodą grzewczą 80℃ - wężownica górna, Wydajność stała (przy podgrzewie cwu z 10 na 60℃) i temperaturze na zasilaniu wodą grzewczą 90℃ - wężownica dolna, Wydajność stała (przy podgrzewie cwu z 10 na 60℃) i temperaturze na zasilaniu wodą grzewczą 90℃ - wężownica górna — the stored unit's dimension contradicts the parameter name (converter mislabeling)

note: [stored X ft] marks values corroborated as IEEE doubles in the binary element streams (Revit-internal decimal feet)
